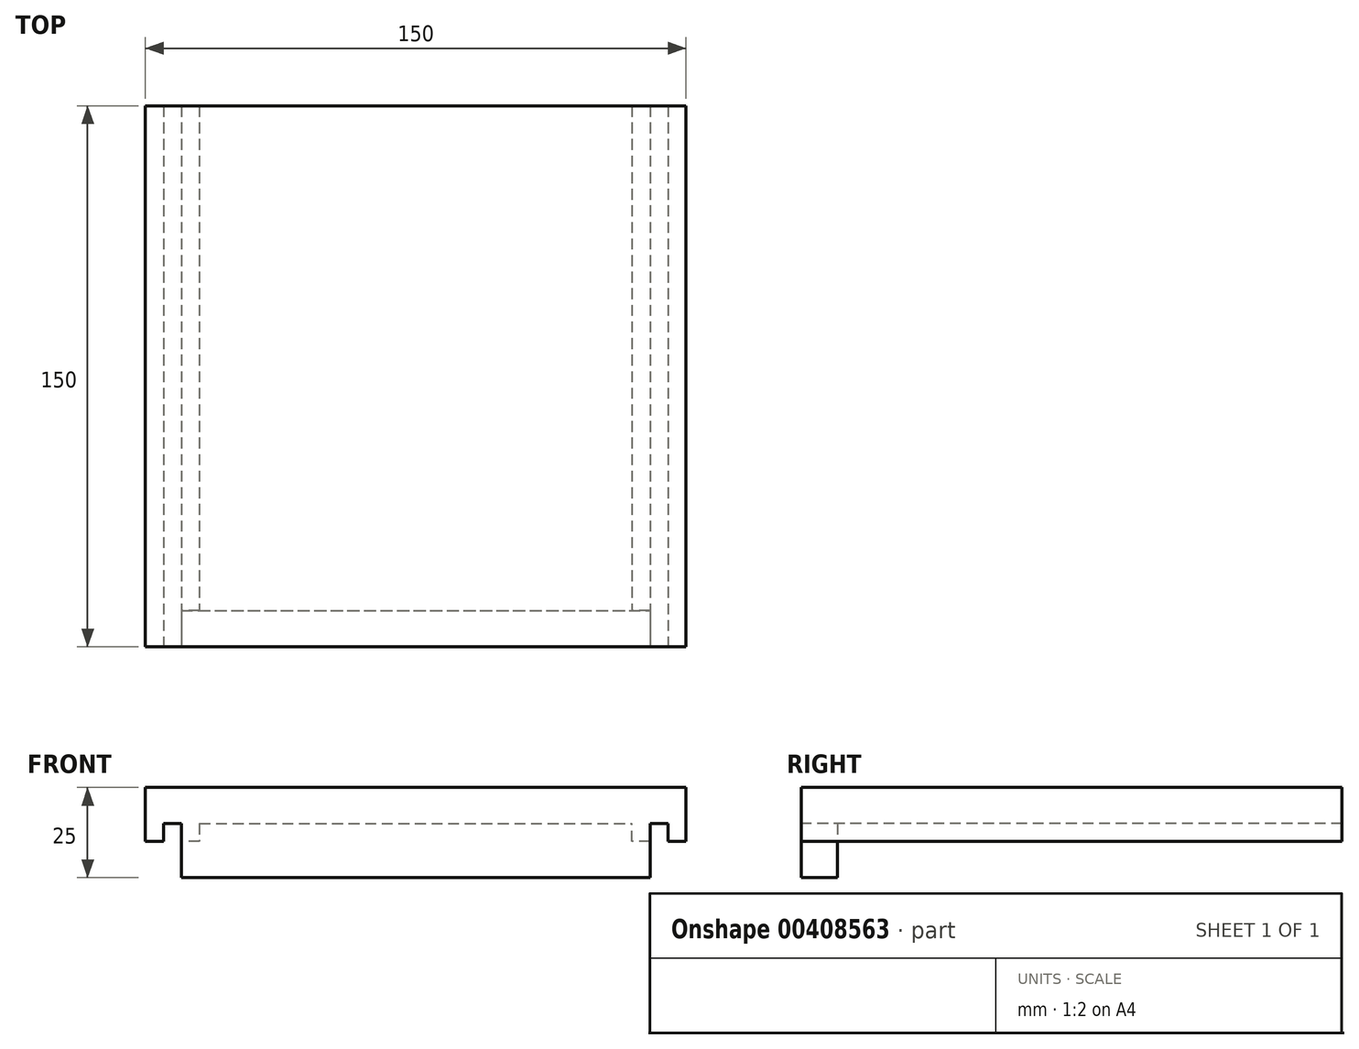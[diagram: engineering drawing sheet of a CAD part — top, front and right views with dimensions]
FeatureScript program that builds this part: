
annotation { "Feature Type Name" : "Feature", "Feature Type Description" : "" }
export const myFeature = defineFeature(function(context is Context, id is Id, definition is map)
    precondition{}
    {
        {
            var Q0;
            Q0=qCreatedBy(makeId("Front.planeOp"),FACE);
            var sketch = newSketch(context, id + "F0", { "sketchPlane" : qUnion([Q0])});
            skLineSegment(sketch, "E0.bottom", {"start": v(-48.5, 39.23) * mm, "end": v(101.5, 39.23) * mm});
            skLineSegment(sketch, "E0.top", {"start": v(-48.5, 24.23) * mm, "end": v(-43.5, 24.23) * mm});
            skLineSegment(sketch, "E0.left", {"start": v(-48.5, 39.23) * mm, "end": v(-48.5, 24.23) * mm});
            skLineSegment(sketch, "E0.right", {"start": v(101.5, 39.23) * mm, "end": v(101.5, 24.23) * mm});
            skLineSegment(sketch, "E1", {"start": v(-43.5, 24.23) * mm, "end": v(-43.5, 29.23) * mm});
            skLineSegment(sketch, "E2", {"start": v(-43.5, 29.23) * mm, "end": v(-38.5, 29.23) * mm});
            skLineSegment(sketch, "E3", {"start": v(-38.5, 29.23) * mm, "end": v(-38.5, 24.23) * mm});
            skLineSegment(sketch, "E4", {"start": v(-38.5, 24.23) * mm, "end": v(-33.5, 24.23) * mm});
            skLineSegment(sketch, "E5", {"start": v(-33.5, 24.23) * mm, "end": v(-33.5, 29.23) * mm});
            skLineSegment(sketch, "E6", {"start": v(-33.5, 29.23) * mm, "end": v(86.5, 29.23) * mm});
            skLineSegment(sketch, "E7", {"start": v(86.5, 29.23) * mm, "end": v(86.5, 24.23) * mm});
            skLineSegment(sketch, "E8", {"start": v(86.5, 24.23) * mm, "end": v(91.5, 24.23) * mm});
            skLineSegment(sketch, "E9", {"start": v(91.5, 24.23) * mm, "end": v(91.5, 29.23) * mm});
            skLineSegment(sketch, "E10", {"start": v(91.5, 29.23) * mm, "end": v(96.5, 29.23) * mm});
            skLineSegment(sketch, "E11", {"start": v(96.5, 29.23) * mm, "end": v(96.5, 24.23) * mm});
            skLineSegment(sketch, "E12.trimOffspring", {"start": v(96.5, 24.23) * mm, "end": v(101.5, 24.23) * mm});
            skLineSegment(sketch, "E13", {"start": v(-48.5, 29.23) * mm, "end": v(101.5, 29.23) * mm, "construction": true});
            skLineSegment(sketch, "E14", {"start": v(-48.5, 24.23) * mm, "end": v(101.5, 24.23) * mm, "construction": true});
            skSolve(sketch);
        }
        {
            var Q0;
            Q0 = qSketchRegion(id + "F0", true);
            extrude(context, id + "F1", {"entities" : qUnion([Q0]), "oppositeDirection" : true, "depth" : 150 * mm});
        }
        {
            var Q0;
            Q0=makeQuery(id+"F1.opExtrude","CAP_FACE",FACE,{"disambiguationData":[OSD([sQuery(id+"F0.wireOp",EDGE,"E0.bottom"),sQuery(id+"F0.wireOp",EDGE,"E0.top"),sQuery(id+"F0.wireOp",EDGE,"E0.left"),sQuery(id+"F0.wireOp",EDGE,"E0.right"),sQuery(id+"F0.wireOp",EDGE,"E1"),sQuery(id+"F0.wireOp",EDGE,"E2"),sQuery(id+"F0.wireOp",EDGE,"E3"),sQuery(id+"F0.wireOp",EDGE,"E5"),sQuery(id+"F0.wireOp",EDGE,"E6"),sQuery(id+"F0.wireOp",EDGE,"E7"),sQuery(id+"F0.wireOp",EDGE,"E9"),sQuery(id+"F0.wireOp",EDGE,"E10"),sQuery(id+"F0.wireOp",EDGE,"E11"),sQuery(id+"F0.wireOp",EDGE,"E8"),sQuery(id+"F0.wireOp",EDGE,"E4"),sQuery(id+"F0.wireOp",EDGE,"E12.trimOffspring")])],"isStart":true});
            var sketch = newSketch(context, id + "F2", { "sketchPlane" : qUnion([Q0])});
            skLineSegment(sketch, "E15.bottom", {"start": v(-38.5, 29.23) * mm, "end": v(91.5, 29.23) * mm});
            skLineSegment(sketch, "E15.top", {"start": v(-38.5, 14.23) * mm, "end": v(91.5, 14.23) * mm});
            skLineSegment(sketch, "E15.left", {"start": v(-38.5, 29.23) * mm, "end": v(-38.5, 14.23) * mm});
            skLineSegment(sketch, "E15.right", {"start": v(91.5, 29.23) * mm, "end": v(91.5, 14.23) * mm});
            skSolve(sketch);
        }
        {
            var Q0;
            Q0 = qSketchRegion(id + "F2", true);
            extrude(context, id + "F3", {"entities" : qUnion([Q0]), "operationType" : NewBodyOperationType.ADD, "oppositeDirection" : true, "depth" : 10 * mm});
        }
    });
